# Revit family: PX_WHB_LECICO_Adesso-Nile_PC-CTOP028
name_source: partatom
category: Plumbing Fixtures
revit_build: Autodesk Revit 2016 (Build: 20190507_1515(x64)
units: mm (PartAtom-declared; Revit-internal decimal feet)

## family parameters
Always vertical = Yes
Cut with Voids When Loaded = No
OmniClass Number = 23.45.05.14.31.11
OmniClass Title = Patients Combination Toilets
Part Type = Normal
Room Calculation Point = No
Round Connector Dimension = Use Diameter
Shared = No
Work Plane-Based = No

## types (1)
- LECICO WHB Adesso Nile PC CTOP028
    Manufacturer = Lecico (Pty) Ltd
    Model = CTOP028
    Tolani Civil Projects cc = www.tcpbim.co.za
    Type Comments = ASIN WEIGHT: 8.9 KG
TAP HOLE OPTIONS: NONE
ASIN WEIGHT: 8.9 KG
TAP HOLE OPTIONS: NONE
TAP HOLE OPTIONS: NONE
    URL = https://www.lecicosa.co.za
    WCPorcelain = Adesso Porcelain
    WHB Height = 750 mm  [stored 2.46063 ft]
    Weight WC = 8.90 kg

note: [stored X ft] marks values corroborated as IEEE doubles in the binary element streams (Revit-internal decimal feet)

## geometry (parser evidence)
native form markers: Sweep x3
no freeform markers — native parametric forms only
